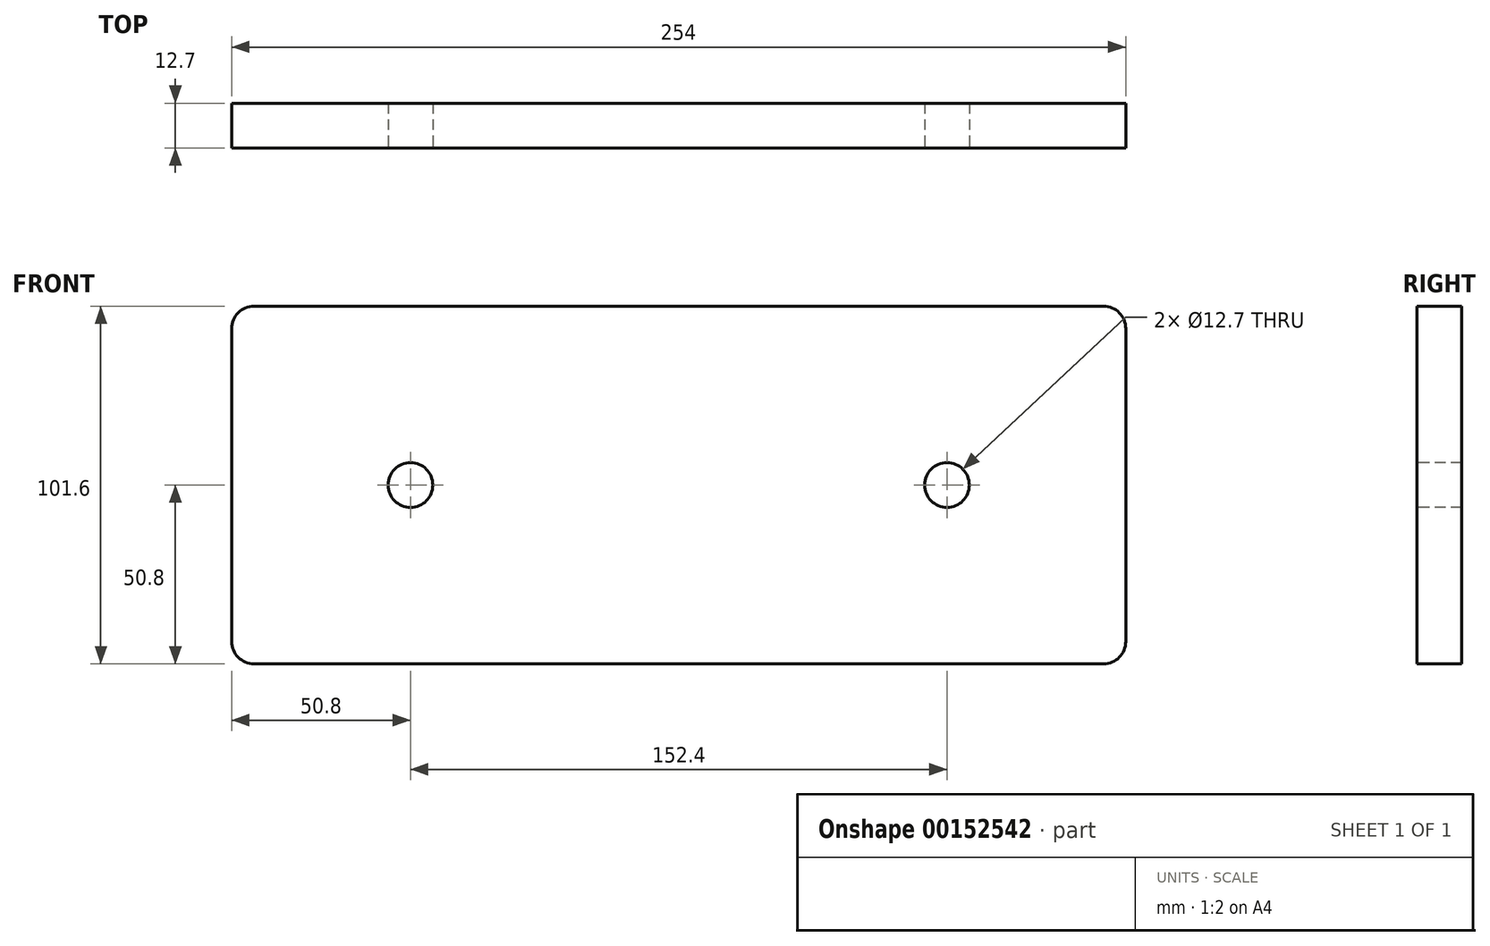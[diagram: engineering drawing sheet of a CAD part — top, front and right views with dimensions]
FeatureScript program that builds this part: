
annotation { "Feature Type Name" : "Feature", "Feature Type Description" : "" }
export const myFeature = defineFeature(function(context is Context, id is Id, definition is map)
    precondition{}
    {
        {
            var Q0;
            Q0=qCreatedBy(makeId("Front.planeOp"),FACE);
            var sketch = newSketch(context, id + "F0", { "sketchPlane" : qUnion([Q0])});
            skLineSegment(sketch, "E0.bottom", {"start": v(0, 0) * mm, "end": v(254, 0) * mm});
            skLineSegment(sketch, "E0.top", {"start": v(0, 101.6) * mm, "end": v(254, 101.6) * mm});
            skLineSegment(sketch, "E0.left", {"start": v(0, 0) * mm, "end": v(0, 101.6) * mm});
            skLineSegment(sketch, "E0.right", {"start": v(254, 0) * mm, "end": v(254, 101.6) * mm});
            skSolve(sketch);
        }
        {
            var Q0;
            Q0 = qSketchRegion(id + "F0", true);
            extrude(context, id + "F1", {"entities" : qUnion([Q0]), "depth" : 12.7 * mm});
        }
        {
            var Q0;
            Q0=makeQuery(id+"F1.opExtrude","SWEPT_EDGE",EDGE,{"disambiguationData":[OSD([sQuery(id+"F0.wireOp",EDGE,"E0.top"),sQuery(id+"F0.wireOp",EDGE,"E0.left")])]});
            var Q1;
            Q1=makeQuery(id+"F1.opExtrude","SWEPT_EDGE",EDGE,{"disambiguationData":[OSD([sQuery(id+"F0.wireOp",EDGE,"E0.bottom"),sQuery(id+"F0.wireOp",EDGE,"E0.left")])]});
            var Q2;
            Q2=makeQuery(id+"F1.opExtrude","SWEPT_EDGE",EDGE,{"disambiguationData":[OSD([sQuery(id+"F0.wireOp",EDGE,"E0.bottom"),sQuery(id+"F0.wireOp",EDGE,"E0.right")])]});
            var Q3;
            Q3=makeQuery(id+"F1.opExtrude","SWEPT_EDGE",EDGE,{"disambiguationData":[OSD([sQuery(id+"F0.wireOp",EDGE,"E0.top"),sQuery(id+"F0.wireOp",EDGE,"E0.right")])]});
            fillet(context, id + "F2", {"entities" : qUnion([Q0, Q1, Q2, Q3]), "radius" : 6.35 * mm, "tangentPropagation" : true, "allowEdgeOverflow" : false});
        }
        {
            var Q0;
            Q0=makeQuery(id+"F1.opExtrude","CAP_FACE",FACE,{"disambiguationData":[OSD([sQuery(id+"F0.wireOp",EDGE,"E0.bottom"),sQuery(id+"F0.wireOp",EDGE,"E0.top"),sQuery(id+"F0.wireOp",EDGE,"E0.left"),sQuery(id+"F0.wireOp",EDGE,"E0.right")])],"isStart":false});
            var sketch = newSketch(context, id + "F3", { "sketchPlane" : qUnion([Q0])});
            skCircle(sketch, "E1", {"center": v(50.8, 50.8) * mm, "radius": 6.35 * mm});
            skPoint(sketch, "E1.centerSnap0", {"position": v(0, 50.8) * mm});
            skCircle(sketch, "E2", {"center": v(203.2, 50.8) * mm, "radius": 6.35 * mm});
            skPoint(sketch, "E2.centerSnap0", {"position": v(254, 50.8) * mm});
            skSolve(sketch);
        }
        {
            var Q0;
            Q0 = qSketchRegion(id + "F3", true);
            extrude(context, id + "F4", {"entities" : qUnion([Q0]), "operationType" : NewBodyOperationType.REMOVE, "endBound" : BoundingType.THROUGH_ALL, "oppositeDirection" : true, "depth" : 25.4 * mm});
        }
    });
